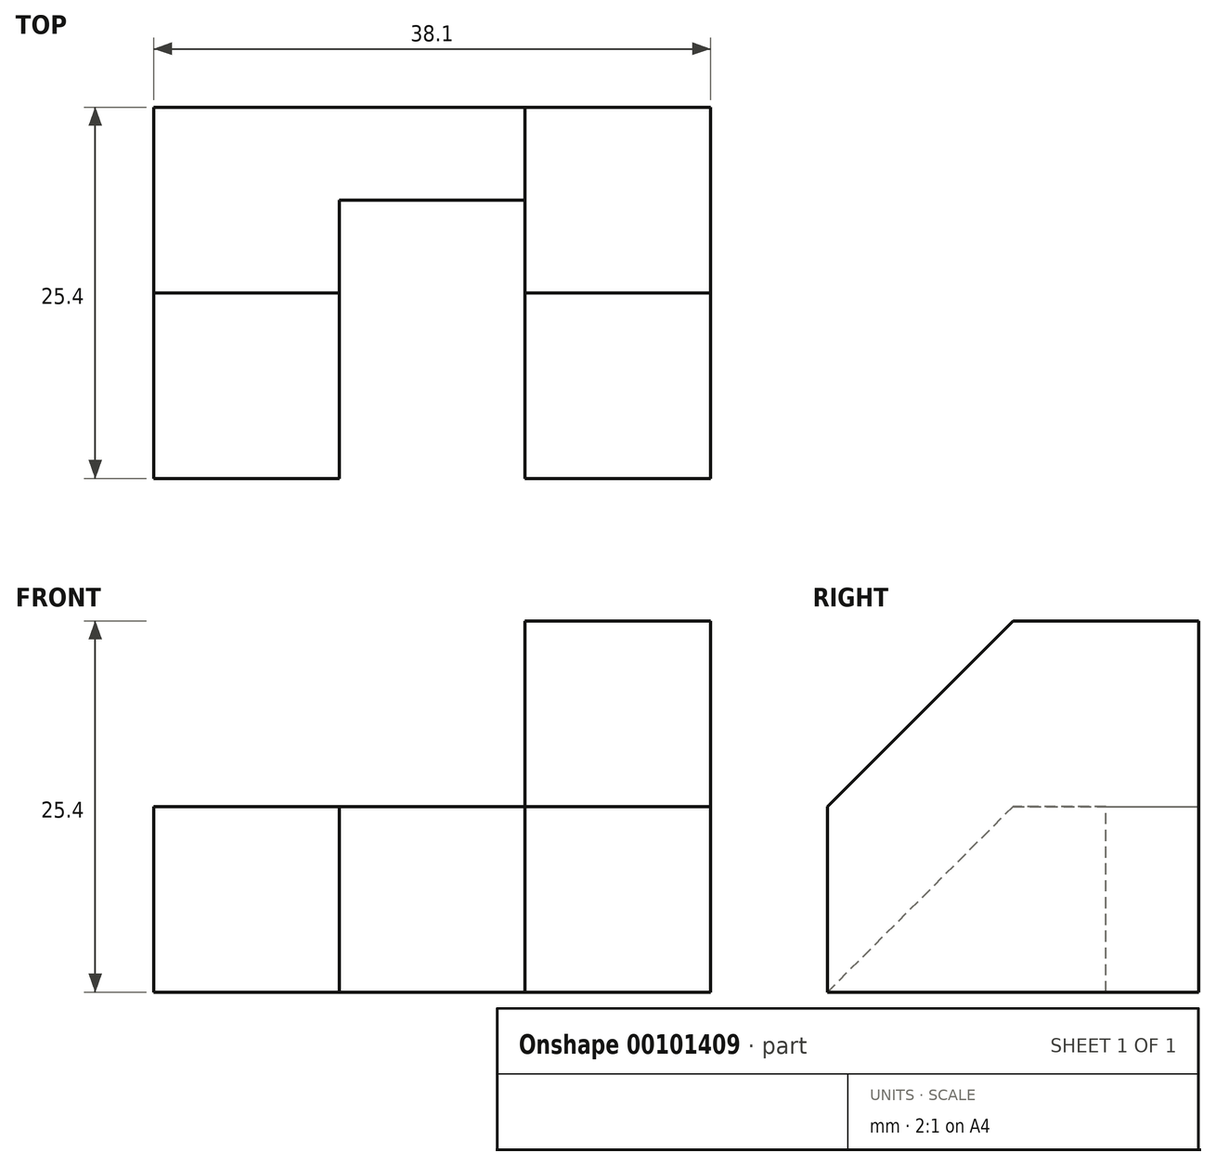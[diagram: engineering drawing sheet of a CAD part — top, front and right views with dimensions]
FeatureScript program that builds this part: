
annotation { "Feature Type Name" : "Feature", "Feature Type Description" : "" }
export const myFeature = defineFeature(function(context is Context, id is Id, definition is map)
    precondition{}
    {
        {
            var Q0;
            Q0=qCreatedBy(makeId("Right.planeOp"),FACE);
            var sketch = newSketch(context, id + "F0", { "sketchPlane" : qUnion([Q0])});
            skLineSegment(sketch, "E0", {"start": v(0, 0) * mm, "end": v(25.4, 0) * mm});
            skLineSegment(sketch, "E1", {"start": v(25.4, 0) * mm, "end": v(25.4, 25.4) * mm});
            skLineSegment(sketch, "E2", {"start": v(25.4, 25.4) * mm, "end": v(12.7, 25.4) * mm});
            skLineSegment(sketch, "E3", {"start": v(12.7, 25.4) * mm, "end": v(0, 12.7) * mm});
            skLineSegment(sketch, "E4", {"start": v(0, 12.7) * mm, "end": v(0, 0) * mm});
            skSolve(sketch);
        }
        {
            var Q0;
            Q0 = qSketchRegion(id + "F0", true);
            extrude(context, id + "F1", {"entities" : qUnion([Q0]), "depth" : 12.7 * mm});
        }
        {
            var Q0;
            Q0=makeQuery(id+"F1.opExtrude","SWEPT_FACE",FACE,{"disambiguationData":[OSD([sQuery(id+"F0.wireOp",EDGE,"E1")])]});
            var sketch = newSketch(context, id + "F2", { "sketchPlane" : qUnion([Q0])});
            skLineSegment(sketch, "E5", {"start": v(0, 0) * mm, "end": v(25.4, 0) * mm});
            skLineSegment(sketch, "E6", {"start": v(25.4, 0) * mm, "end": v(25.4, 12.7) * mm});
            skLineSegment(sketch, "E7", {"start": v(25.4, 12.7) * mm, "end": v(0, 12.7) * mm});
            skLineSegment(sketch, "E8", {"start": v(0, 12.7) * mm, "end": v(0, 0) * mm});
            skSolve(sketch);
        }
        {
            var Q0;
            Q0=makeQuery(id+"F2.imprint","IMPRINT",FACE,{"disambiguationData":[TD([[makeQuery(id+"F2.imprint","IMPRINT",EDGE,{"derivedFrom":sQuery(id+"F2.wireOp",EDGE,"E5")}),1.0]])]});
            extrude(context, id + "F3", {"entities" : qUnion([Q0]), "operationType" : NewBodyOperationType.ADD, "oppositeDirection" : true, "depth" : 6.35 * mm});
        }
        {
            var Q0;
            Q0=makeQuery(id+"F3.opExtrude","SWEPT_FACE",FACE,{"disambiguationData":[OSD([sQuery(id+"F2.wireOp",EDGE,"E6")])]});
            var sketch = newSketch(context, id + "F4", { "sketchPlane" : qUnion([Q0])});
            skLineSegment(sketch, "E9", {"start": v(-19.05, 0) * mm, "end": v(0, 0) * mm});
            skLineSegment(sketch, "E10", {"start": v(-19.05, 0) * mm, "end": v(-19.05, 12.7) * mm});
            skLineSegment(sketch, "E11", {"start": v(-19.05, 12.7) * mm, "end": v(-12.7, 12.7) * mm});
            skLineSegment(sketch, "E12", {"start": v(-12.7, 12.7) * mm, "end": v(0, 0) * mm});
            skSolve(sketch);
        }
        {
            var Q0;
            Q0 = qSketchRegion(id + "F4", true);
            extrude(context, id + "F5", {"entities" : qUnion([Q0]), "operationType" : NewBodyOperationType.ADD, "oppositeDirection" : true, "depth" : 12.7 * mm});
        }
    });
